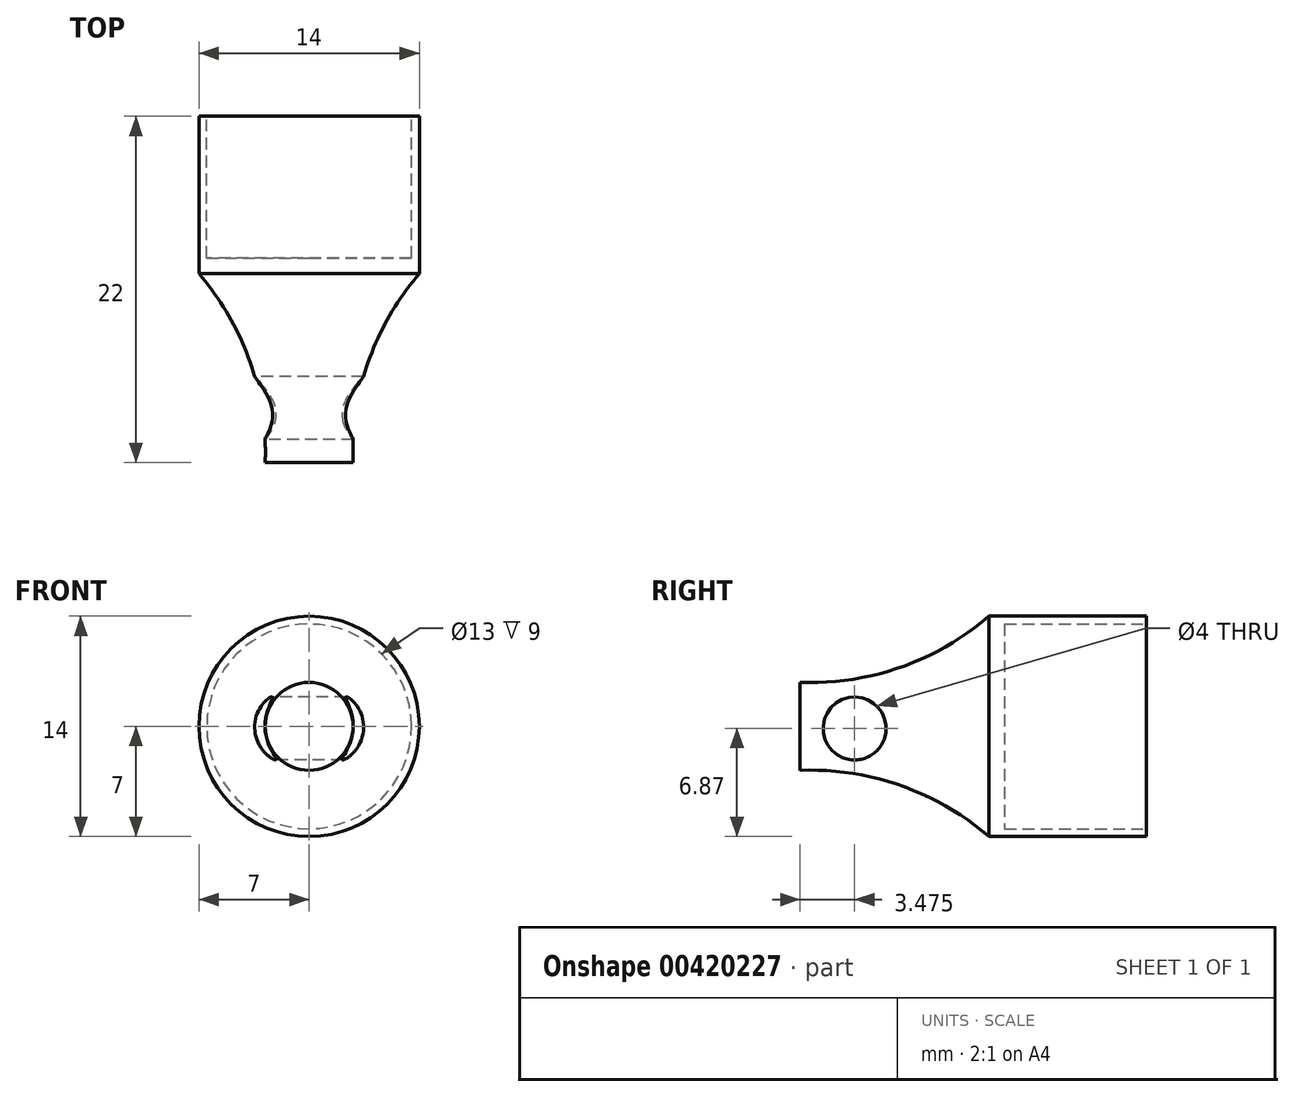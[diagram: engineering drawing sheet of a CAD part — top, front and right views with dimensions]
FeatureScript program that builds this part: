
annotation { "Feature Type Name" : "Feature", "Feature Type Description" : "" }
export const myFeature = defineFeature(function(context is Context, id is Id, definition is map)
    precondition{}
    {
        {
            var Q0;
            Q0=qCreatedBy(makeId("Top.planeOp"),FACE);
            var sketch = newSketch(context, id + "F0", { "sketchPlane" : qUnion([Q0])});
            skPoint(sketch, "E0.orphan", {"position": v(0, -68) * mm});
            skLineSegment(sketch, "E1.MirrorCS", {"start": v(0, -68) * mm, "end": v(0, -58) * mm});
            skArc(sketch, "E2.MirrorCS", {"start": v(0, -68) * mm, "mid": v(3.24, -73.6) * mm, "end": v(4.2, -80) * mm});
            skLineSegment(sketch, "E3.MirrorCS", {"start": v(7, -80) * mm, "end": v(4.2, -80) * mm});
            skLineSegment(sketch, "E4.MirrorCS", {"start": v(7, -80) * mm, "end": v(7, -57) * mm});
            skLineSegment(sketch, "E5", {"start": v(0, -58) * mm, "end": v(7, -58) * mm});
            skPoint(sketch, "E5.endSnap0", {"position": v(7, -57) * mm});
            skPoint(sketch, "E6.orphan", {"position": v(0, -34) * mm});
            skPoint(sketch, "E7.orphan", {"position": v(7, -34) * mm});
            skPoint(sketch, "E8.start.orphan", {"position": v(0, 0) * mm});
            skSolve(sketch);
        }
        {
            var Q0;
            Q0=makeQuery(id+"F0.imprint","IMPRINT",FACE,{"disambiguationData":[TD([[makeQuery(id+"F0.imprint","IMPRINT",EDGE,{"derivedFrom":sQuery(id+"F0.wireOp",EDGE,"E1.MirrorCS")}),-1.0]])]});
            var Q1;
            Q1=sQuery(id+"F0.wireOp",EDGE,"E4.MirrorCS");
            revolve(context, id + "F1", {"entities" : qUnion([Q0]), "axis" : qUnion([Q1]), "revolveType" : RevolveType.FULL});
        }
        {
            var Q0;
            Q0=qCreatedBy(makeId("Right.planeOp"),FACE);
            var sketch = newSketch(context, id + "F2", { "sketchPlane" : qUnion([Q0])});
            skCircle(sketch, "E9", {"center": v(-76.52, -0.13) * mm, "radius": 2 * mm});
            skSolve(sketch);
        }
        {
            var Q0;
            Q0=makeQuery(id+"F2.imprint","IMPRINT",FACE,{"disambiguationData":[TD([[makeQuery(id+"F2.imprint","IMPRINT",EDGE,{"derivedFrom":sQuery(id+"F2.wireOp",EDGE,"E9")}),1.0]])]});
            extrude(context, id + "F3", {"entities" : qUnion([Q0]), "operationType" : NewBodyOperationType.REMOVE, "depth" : 25.4 * mm, "offsetDistance" : 25.4 * mm});
        }
        {
            var Q0;
            Q0=makeQuery(id+"F1.opRevolve","SWEPT_FACE",FACE,{"disambiguationData":[OSD([sQuery(id+"F0.wireOp",EDGE,"E5")])]});
            var sketch = newSketch(context, id + "F4", { "sketchPlane" : qUnion([Q0])});
            skCircle(sketch, "E10", {"center": v(-7, 0) * mm, "radius": 6.5 * mm});
            skSolve(sketch);
        }
        {
            var Q0;
            Q0=makeQuery(id+"F4.imprint","IMPRINT",FACE,{"disambiguationData":[TD([[makeQuery(id+"F4.imprint","IMPRINT",EDGE,{"derivedFrom":sQuery(id+"F4.wireOp",EDGE,"E10")}),1.0]])]});
            extrude(context, id + "F5", {"entities" : qUnion([Q0]), "operationType" : NewBodyOperationType.REMOVE, "oppositeDirection" : true, "depth" : 9 * mm, "offsetDistance" : 25.4 * mm});
        }
    });
